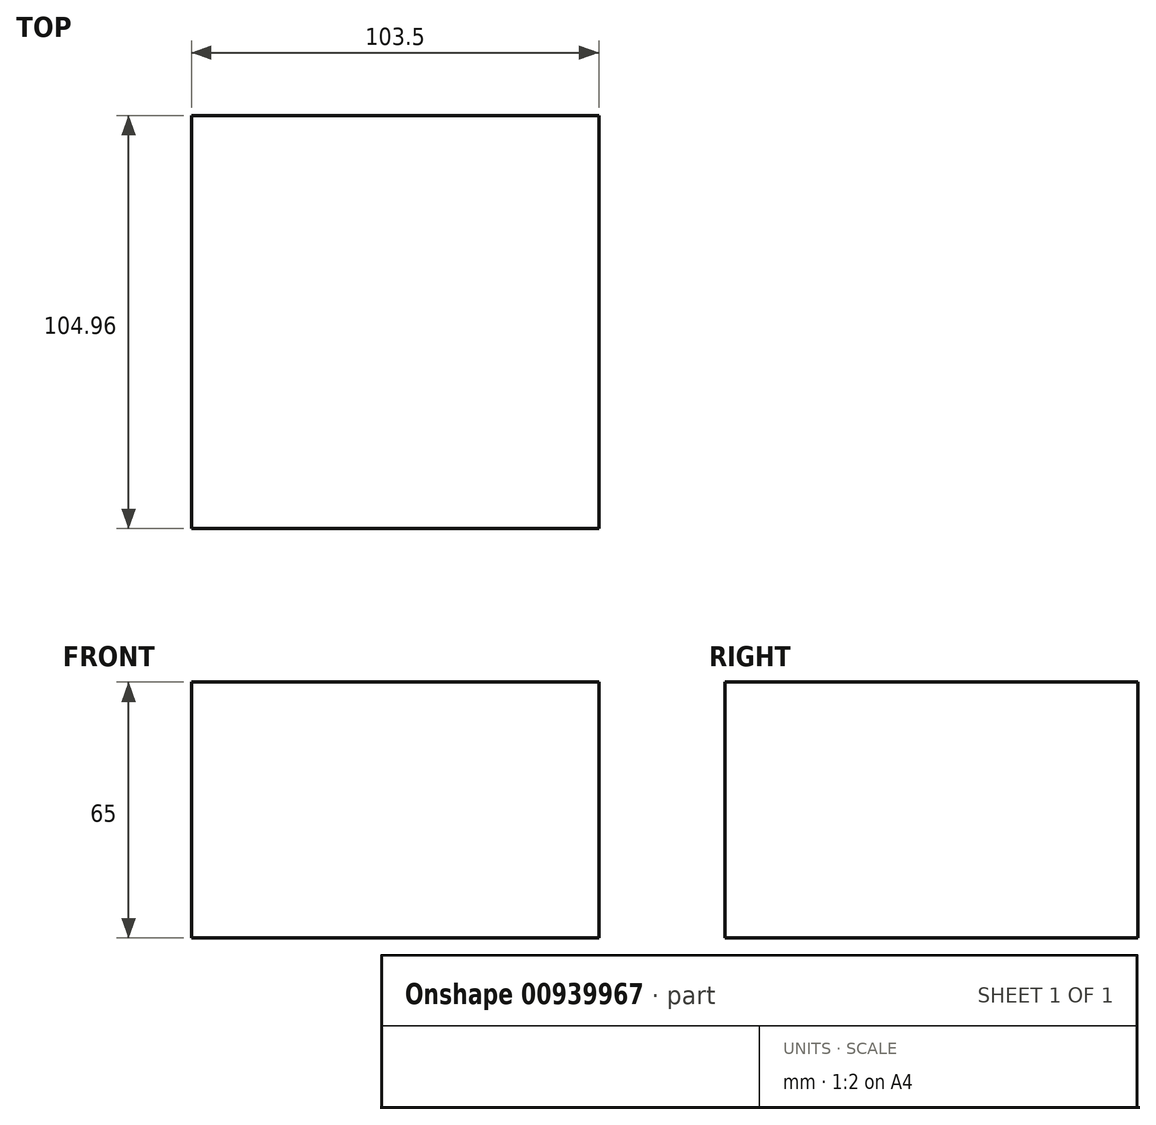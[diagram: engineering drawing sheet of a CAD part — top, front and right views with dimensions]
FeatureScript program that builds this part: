
annotation { "Feature Type Name" : "Feature", "Feature Type Description" : "" }
export const myFeature = defineFeature(function(context is Context, id is Id, definition is map)
    precondition{}
    {
        {
            var Q0;
            Q0=qCreatedBy(makeId("Top.planeOp"),FACE);
            var sketch = newSketch(context, id + "F0", { "sketchPlane" : qUnion([Q0])});
            skLineSegment(sketch, "E0.bottom", {"start": v(0, 0) * mm, "end": v(-103.5, 0) * mm});
            skLineSegment(sketch, "E0.top", {"start": v(0, 104.96) * mm, "end": v(-103.5, 104.96) * mm});
            skLineSegment(sketch, "E0.left", {"start": v(0, 0) * mm, "end": v(0, 104.96) * mm});
            skLineSegment(sketch, "E0.right", {"start": v(-103.5, 0) * mm, "end": v(-103.5, 104.96) * mm});
            skSolve(sketch);
        }
        {
            var Q0;
            Q0 = qSketchRegion(id + "F0", true);
            extrude(context, id + "F1", {"entities" : qUnion([Q0]), "depth" : 65 * mm, "offsetDistance" : 25 * mm});
        }
    });
